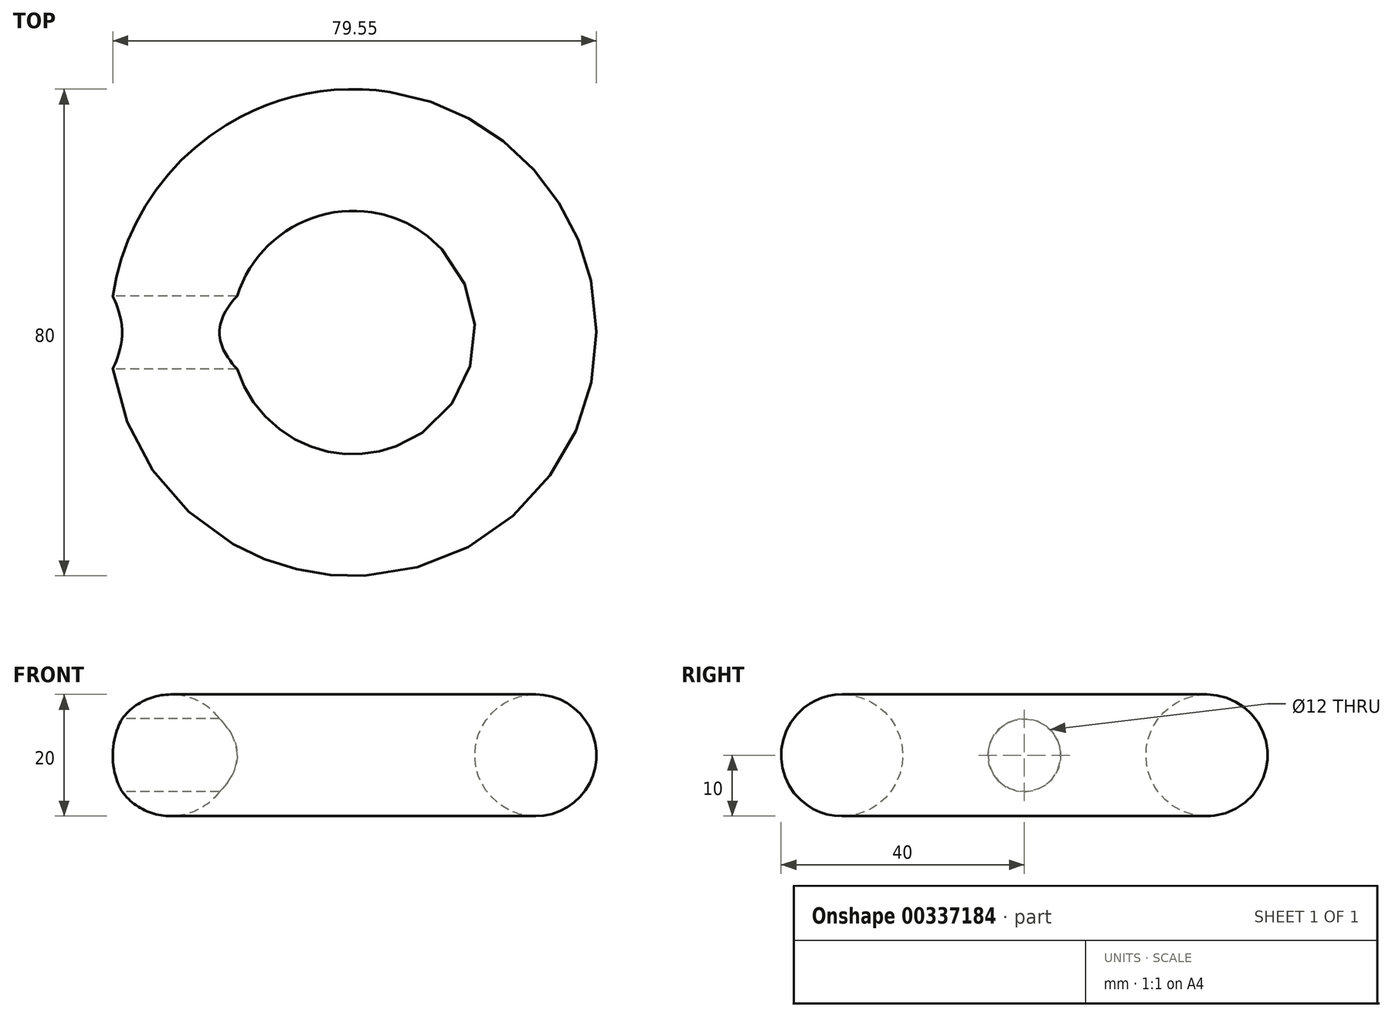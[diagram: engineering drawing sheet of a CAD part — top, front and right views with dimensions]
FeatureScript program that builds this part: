
annotation { "Feature Type Name" : "Feature", "Feature Type Description" : "" }
export const myFeature = defineFeature(function(context is Context, id is Id, definition is map)
    precondition{}
    {
        {
            var Q0;
            Q0=qCreatedBy(makeId("Front.planeOp"),FACE);
            var sketch = newSketch(context, id + "F0", { "sketchPlane" : qUnion([Q0])});
            skCircle(sketch, "E0", {"center": v(0, 0) * mm, "radius": 10 * mm});
            skLineSegment(sketch, "E1", {"start": v(30, 0) * mm, "end": v(30, 20.85) * mm});
            skLineSegment(sketch, "E2", {"start": v(30, 20.85) * mm, "end": v(30, 0) * mm});
            skLineSegment(sketch, "E3", {"start": v(30, -16.53) * mm, "end": v(30, 0) * mm});
            skSolve(sketch);
        }
        {
            var Q0;
            Q0=makeQuery(id+"F0.imprint","IMPRINT",FACE,{"disambiguationData":[TD([[makeQuery(id+"F0.imprint","IMPRINT",EDGE,{"derivedFrom":sQuery(id+"F0.wireOp",EDGE,"E0")}),1.0]])]});
            var Q1;
            Q1=sQuery(id+"F0.wireOp",EDGE,"E2");
            revolve(context, id + "F1", {"entities" : qUnion([Q0]), "axis" : qUnion([Q1]), "revolveType" : RevolveType.FULL});
        }
        {
            var Q0;
            Q0=qCreatedBy(makeId("Top.planeOp"),FACE);
            var sketch = newSketch(context, id + "F2", { "sketchPlane" : qUnion([Q0])});
            skLineSegment(sketch, "E4", {"start": v(30, 0) * mm, "end": v(30, 40) * mm});
            skLineSegment(sketch, "E5", {"start": v(30, 0) * mm, "end": v(66.04, 17.36) * mm});
            skLineSegment(sketch, "E6", {"start": v(30, 0) * mm, "end": v(38.9, -39) * mm});
            skLineSegment(sketch, "E7", {"start": v(30, 0) * mm, "end": v(5.06, -31.27) * mm});
            skLineSegment(sketch, "E8", {"start": v(30, 0) * mm, "end": v(5.06, 31.27) * mm});
            skLineSegment(sketch, "E9", {"start": v(30, 0) * mm, "end": v(-10, 0) * mm});
            skLineSegment(sketch, "E10", {"start": v(30, 0) * mm, "end": v(66.04, -17.36) * mm});
            skSolve(sketch);
        }
        {
            var Q0;
            Q0=qCreatedBy(makeId("Top.planeOp"),FACE);
            var sketch = newSketch(context, id + "F3", { "sketchPlane" : qUnion([Q0])});
            skLineSegment(sketch, "E11", {"start": v(30, 0) * mm, "end": v(30, -41) * mm});
            skSolve(sketch);
        }
        {
            var Q0;
            Q0=qCreatedBy(makeId("Right.planeOp"),FACE);
            cPlane(context, id + "F4", {"entities" : qUnion([Q0]), "cplaneType" : CPlaneType.OFFSET, "offset" : 10 * mm, "oppositeDirection" : true, "width" : 150 * mm, "height" : 150 * mm});
        }
        {
            var Q0;
            Q0=qCreatedBy(id+"F4.planeOp",FACE);
            var sketch = newSketch(context, id + "F5", { "sketchPlane" : qUnion([Q0])});
            skCircle(sketch, "E12", {"center": v(0, 0) * mm, "radius": 6 * mm});
            skSolve(sketch);
        }
        {
            var Q0;
            Q0=makeQuery(id+"F5.imprint","IMPRINT",FACE,{"disambiguationData":[TD([[makeQuery(id+"F5.imprint","IMPRINT",EDGE,{"derivedFrom":sQuery(id+"F5.wireOp",EDGE,"E12")}),1.0]])]});
            extrude(context, id + "F6", {"entities" : qUnion([Q0]), "operationType" : NewBodyOperationType.REMOVE, "depth" : 25 * mm});
        }
    });
